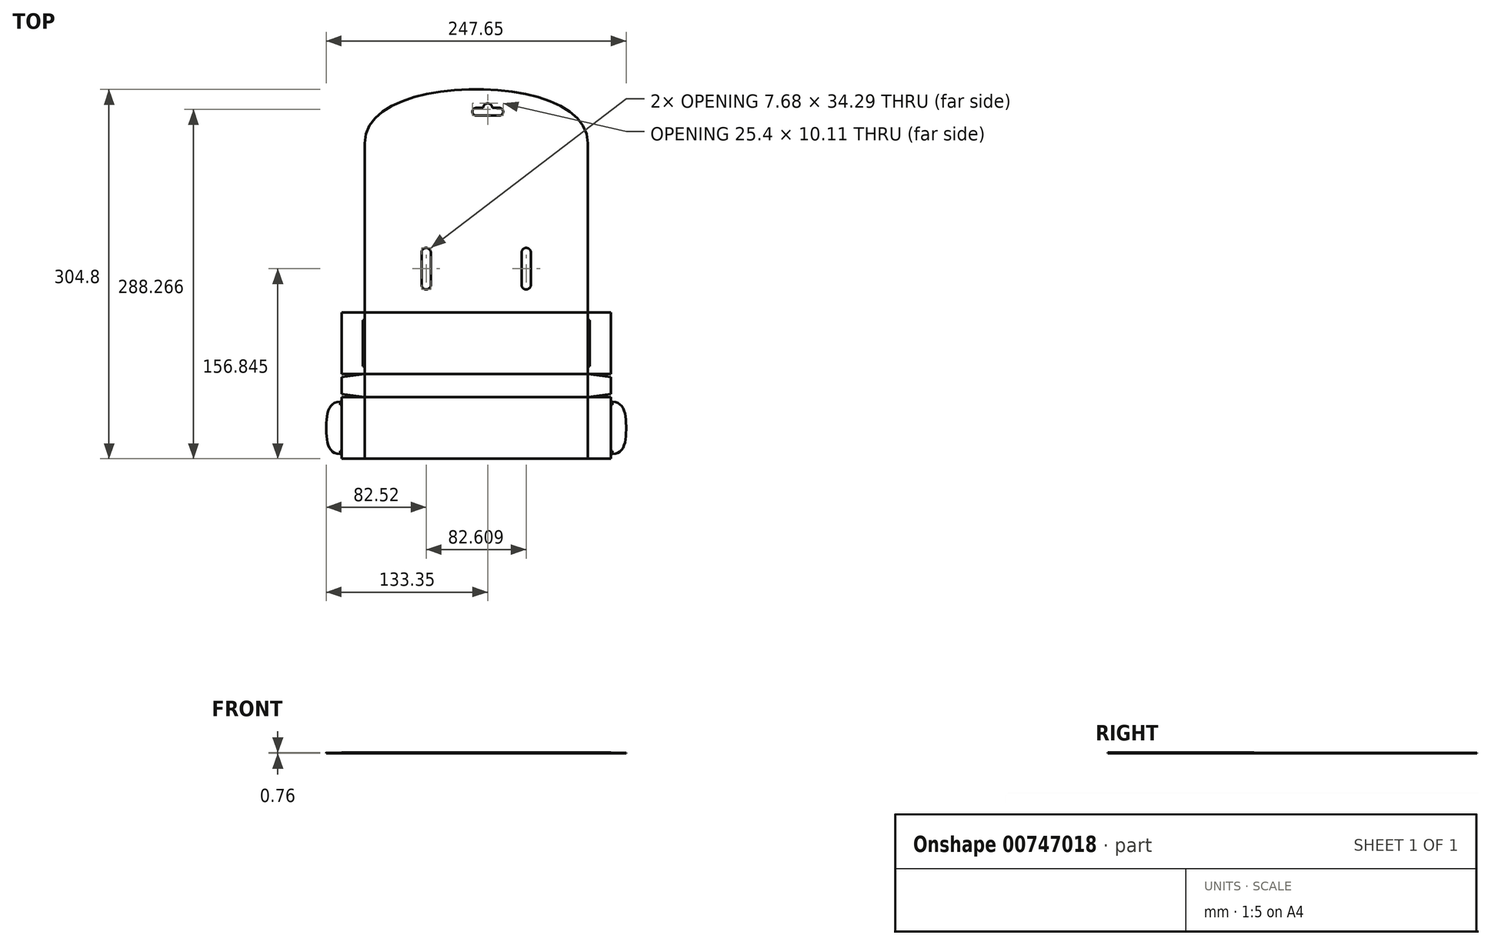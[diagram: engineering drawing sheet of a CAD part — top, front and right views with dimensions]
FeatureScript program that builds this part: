
annotation { "Feature Type Name" : "Feature", "Feature Type Description" : "" }
export const myFeature = defineFeature(function(context is Context, id is Id, definition is map)
    precondition{}
    {
        {
            var Q0;
            Q0=qCreatedBy(makeId("Top.planeOp"),FACE);
            var sketch = newSketch(context, id + "F0", { "sketchPlane" : qUnion([Q0])});
            skLineSegment(sketch, "E0", {"start": v(0, 0) * mm, "end": v(184.15, 0) * mm});
            skLineSegment(sketch, "E1", {"start": v(184.15, 0) * mm, "end": v(184.15, 50.8) * mm});
            skLineSegment(sketch, "E2", {"start": v(184.15, 50.8) * mm, "end": v(203.2, 50.8) * mm});
            skLineSegment(sketch, "E3", {"start": v(203.2, 50.8) * mm, "end": v(203.2, 0) * mm});
            skLineSegment(sketch, "E4", {"start": v(203.2, 0) * mm, "end": v(184.15, 0) * mm});
            skLineSegment(sketch, "E5", {"start": v(184.15, 50.8) * mm, "end": v(0, 50.8) * mm});
            skLineSegment(sketch, "E6", {"start": v(0, 50.8) * mm, "end": v(0, 0) * mm});
            skLineSegment(sketch, "E7", {"start": v(0, 50.8) * mm, "end": v(-19.05, 50.8) * mm});
            skLineSegment(sketch, "E8", {"start": v(-19.05, 50.8) * mm, "end": v(-19.05, 0) * mm});
            skLineSegment(sketch, "E9", {"start": v(-19.05, 0) * mm, "end": v(0, 0) * mm});
            skLineSegment(sketch, "E10", {"start": v(0, 50.8) * mm, "end": v(0, 69.85) * mm});
            skLineSegment(sketch, "E11", {"start": v(0, 69.85) * mm, "end": v(184.15, 69.85) * mm});
            skLineSegment(sketch, "E12", {"start": v(184.15, 69.85) * mm, "end": v(184.15, 50.8) * mm});
            skLineSegment(sketch, "E13", {"start": v(-19.05, 67.3) * mm, "end": v(-19.05, 53.34) * mm});
            skLineSegment(sketch, "E14", {"start": v(-19.05, 67.3) * mm, "end": v(0, 69.85) * mm});
            skLineSegment(sketch, "E15", {"start": v(-19.05, 53.34) * mm, "end": v(0, 50.8) * mm});
            skLineSegment(sketch, "E16", {"start": v(0, 69.85) * mm, "end": v(0, 260.35) * mm});
            skLineSegment(sketch, "E17", {"start": v(0, 260.35) * mm, "end": v(184.15, 260.35) * mm, "construction": true});
            skLineSegment(sketch, "E18", {"start": v(184.15, 260.35) * mm, "end": v(184.15, 69.85) * mm});
            skLineSegment(sketch, "E19.0", {"start": v(0, 120.65) * mm, "end": v(203.2, 120.65) * mm});
            skLineSegment(sketch, "E20", {"start": v(0, 120.65) * mm, "end": v(-19.05, 120.65) * mm});
            skLineSegment(sketch, "E21", {"start": v(-19.05, 120.65) * mm, "end": v(-19.05, 69.85) * mm});
            skLineSegment(sketch, "E22", {"start": v(-19.05, 69.85) * mm, "end": v(0, 69.85) * mm});
            skLineSegment(sketch, "E23", {"start": v(92.08, 0) * mm, "end": v(92.08, 260.35) * mm, "construction": true});
            skLineSegment(sketch, "E24.MirrorCS", {"start": v(203.2, 67.3) * mm, "end": v(203.2, 53.34) * mm});
            skLineSegment(sketch, "E25.MirrorCS", {"start": v(203.2, 67.3) * mm, "end": v(184.15, 69.85) * mm});
            skLineSegment(sketch, "E26.MirrorCS", {"start": v(203.2, 53.34) * mm, "end": v(184.15, 50.8) * mm});
            skLineSegment(sketch, "E27.MirrorCS", {"start": v(203.2, 69.85) * mm, "end": v(184.15, 69.85) * mm});
            skLineSegment(sketch, "E28.MirrorCS", {"start": v(203.2, 120.65) * mm, "end": v(203.2, 69.85) * mm});
            skLineSegment(sketch, "E29.MirrorCS", {"start": v(184.15, 120.65) * mm, "end": v(203.2, 120.65) * mm});
            skFitSpline(sketch, "E30", {"points": [v(0, 260.35) * mm, v(92.08, 304.8) * mm, v(184.15, 260.35) * mm], "startDerivative": vector(0, 185.57) * mm, "endDerivative": vector(0, -185.57) * mm});
            skLineSegment(sketch, "E31", {"start": v(133.4, 224.8) * mm, "end": v(133.4, 174) * mm});
            skLineSegment(sketch, "E32", {"start": v(127.06, 231.14) * mm, "end": v(57.2, 231.14) * mm});
            skLineSegment(sketch, "E33", {"start": v(50.86, 224.8) * mm, "end": v(50.86, 174) * mm});
            skLineSegment(sketch, "E34.0", {"start": v(129.54, 170.18) * mm, "end": v(129.54, 143.51) * mm});
            skLineSegment(sketch, "E35.0", {"start": v(137.22, 170.17) * mm, "end": v(137.16, 143.5) * mm});
            skLineSegment(sketch, "E36", {"start": v(133.35, 139.7) * mm, "end": v(133.35, 139.7) * mm});
            skLineSegment(sketch, "E37", {"start": v(133.35, 173.99) * mm, "end": v(133.4, 174) * mm});
            skLineSegment(sketch, "E38.MirrorCS", {"start": v(54.6, 170.18) * mm, "end": v(54.61, 143.51) * mm});
            skLineSegment(sketch, "E39.MirrorCS", {"start": v(46.93, 170.17) * mm, "end": v(47, 143.5) * mm});
            skLineSegment(sketch, "E40.MirrorCS", {"start": v(50.8, 139.7) * mm, "end": v(50.8, 139.7) * mm});
            skLineSegment(sketch, "E41.MirrorCS", {"start": v(50.8, 173.99) * mm, "end": v(50.74, 174) * mm});
            skPoint(sketch, "E42.visualSharp", {"position": v(129.54, 173.99) * mm});
            skArc(sketch, "E42.filletArc", {"start": v(133.35, 173.99) * mm, "mid": v(130.66, 172.87) * mm, "end": v(129.54, 170.18) * mm});
            skPoint(sketch, "E43.visualSharp", {"position": v(137.23, 174) * mm});
            skArc(sketch, "E43.filletArc", {"start": v(137.22, 170.17) * mm, "mid": v(136.1, 172.87) * mm, "end": v(133.4, 174) * mm});
            skPoint(sketch, "E44.visualSharp", {"position": v(129.54, 139.7) * mm});
            skArc(sketch, "E44.filletArc", {"start": v(129.54, 143.51) * mm, "mid": v(130.66, 140.82) * mm, "end": v(133.35, 139.7) * mm});
            skPoint(sketch, "E45.visualSharp", {"position": v(137.15, 139.7) * mm});
            skArc(sketch, "E45.filletArc", {"start": v(133.35, 139.7) * mm, "mid": v(136.04, 140.81) * mm, "end": v(137.16, 143.5) * mm});
            skPoint(sketch, "E46.visualSharp", {"position": v(54.6, 173.99) * mm});
            skArc(sketch, "E46.filletArc", {"start": v(54.6, 170.18) * mm, "mid": v(53.5, 172.87) * mm, "end": v(50.8, 173.99) * mm});
            skPoint(sketch, "E47.visualSharp", {"position": v(46.92, 174) * mm});
            skArc(sketch, "E47.filletArc", {"start": v(50.74, 174) * mm, "mid": v(48.04, 172.87) * mm, "end": v(46.93, 170.17) * mm});
            skPoint(sketch, "E48.visualSharp", {"position": v(47, 139.7) * mm});
            skArc(sketch, "E48.filletArc", {"start": v(47, 143.5) * mm, "mid": v(48.1, 140.81) * mm, "end": v(50.8, 139.7) * mm});
            skPoint(sketch, "E49.visualSharp", {"position": v(54.61, 139.7) * mm});
            skArc(sketch, "E49.filletArc", {"start": v(50.8, 139.7) * mm, "mid": v(53.5, 140.82) * mm, "end": v(54.61, 143.51) * mm});
            skPoint(sketch, "E50.visualSharp", {"position": v(50.86, 231.14) * mm});
            skArc(sketch, "E50.filletArc", {"start": v(57.2, 231.14) * mm, "mid": v(52.72, 229.28) * mm, "end": v(50.86, 224.8) * mm});
            skPoint(sketch, "E51.visualSharp", {"position": v(133.4, 231.14) * mm});
            skArc(sketch, "E51.filletArc", {"start": v(133.4, 224.8) * mm, "mid": v(131.55, 229.28) * mm, "end": v(127.06, 231.14) * mm});
            skLineSegment(sketch, "E52", {"start": v(184.15, 114.3) * mm, "end": v(185.74, 114.3) * mm});
            skLineSegment(sketch, "E53", {"start": v(185.74, 114.3) * mm, "end": v(185.74, 76.2) * mm});
            skLineSegment(sketch, "E54", {"start": v(185.74, 76.2) * mm, "end": v(184.15, 76.2) * mm});
            skLineSegment(sketch, "E55.MirrorCS", {"start": v(-1.59, 114.3) * mm, "end": v(-1.59, 76.2) * mm});
            skLineSegment(sketch, "E56.MirrorCS", {"start": v(0, 114.3) * mm, "end": v(-1.59, 114.3) * mm});
            skLineSegment(sketch, "E57.MirrorCS", {"start": v(-1.59, 76.2) * mm, "end": v(0, 76.2) * mm});
            skLineSegment(sketch, "E58", {"start": v(-19.05, 3.81) * mm, "end": v(-19.05, 0) * mm});
            skFitSpline(sketch, "E59", {"points": [v(-20.32, 46.99) * mm, v(-31.75, 25.4) * mm, v(-20.32, 3.8) * mm], "startDerivative": vector(-60.96, -1.37) * mm, "endDerivative": vector(60.96, -0.05) * mm});
            skLineSegment(sketch, "E60.0", {"start": v(-20.32, 44.45) * mm, "end": v(-19.05, 44.45) * mm});
            skLineSegment(sketch, "E61.0", {"start": v(-20.32, 6.35) * mm, "end": v(-19.05, 6.35) * mm});
            skLineSegment(sketch, "E62", {"start": v(-20.32, 46.99) * mm, "end": v(-20.32, 44.45) * mm});
            skLineSegment(sketch, "E63", {"start": v(-20.32, 3.8) * mm, "end": v(-20.32, 6.35) * mm});
            skFitSpline(sketch, "E64.MirrorCS", {"points": [v(204.47, 46.99) * mm, v(215.9, 25.4) * mm, v(204.47, 3.8) * mm], "startDerivative": vector(60.96, -1.37) * mm, "endDerivative": vector(-60.96, -0.05) * mm});
            skLineSegment(sketch, "E65.MirrorCS", {"start": v(204.47, 46.99) * mm, "end": v(204.47, 44.45) * mm});
            skLineSegment(sketch, "E66.MirrorCS", {"start": v(204.47, 44.45) * mm, "end": v(203.2, 44.45) * mm});
            skLineSegment(sketch, "E67.MirrorCS", {"start": v(204.47, 3.8) * mm, "end": v(204.47, 6.35) * mm});
            skLineSegment(sketch, "E68.MirrorCS", {"start": v(204.47, 6.35) * mm, "end": v(203.2, 6.35) * mm});
            skLineSegment(sketch, "E69", {"start": v(88.9, 286.39) * mm, "end": v(88.9, 286.39) * mm});
            skLineSegment(sketch, "E70", {"start": v(92.08, 283.21) * mm, "end": v(111.13, 283.21) * mm});
            skLineSegment(sketch, "E71", {"start": v(114.3, 286.39) * mm, "end": v(114.3, 286.39) * mm});
            skLineSegment(sketch, "E72", {"start": v(111.13, 289.56) * mm, "end": v(105.4, 289.56) * mm});
            skLineSegment(sketch, "E73", {"start": v(92.08, 289.56) * mm, "end": v(97.8, 289.56) * mm});
            skArc(sketch, "E74", {"start": v(105.4, 289.56) * mm, "mid": v(101.6, 293.32) * mm, "end": v(97.8, 289.56) * mm});
            skPoint(sketch, "E75.visualSharp", {"position": v(88.9, 289.56) * mm});
            skArc(sketch, "E75.filletArc", {"start": v(92.08, 289.56) * mm, "mid": v(89.83, 288.63) * mm, "end": v(88.9, 286.39) * mm});
            skPoint(sketch, "E76.visualSharp", {"position": v(88.9, 283.21) * mm});
            skArc(sketch, "E76.filletArc", {"start": v(88.9, 286.39) * mm, "mid": v(89.83, 284.14) * mm, "end": v(92.08, 283.21) * mm});
            skPoint(sketch, "E77.visualSharp", {"position": v(114.3, 289.56) * mm});
            skArc(sketch, "E77.filletArc", {"start": v(114.3, 286.39) * mm, "mid": v(113.37, 288.63) * mm, "end": v(111.13, 289.56) * mm});
            skPoint(sketch, "E78.visualSharp", {"position": v(114.3, 283.21) * mm});
            skArc(sketch, "E78.filletArc", {"start": v(111.13, 283.21) * mm, "mid": v(113.37, 284.14) * mm, "end": v(114.3, 286.39) * mm});
            skLineSegment(sketch, "E79", {"start": v(92.08, 304.8) * mm, "end": v(92.08, 260.35) * mm, "construction": true});
            skArc(sketch, "E80", {"start": v(50.8, 139.7) * mm, "mid": v(92.07, 126.94) * mm, "end": v(133.35, 139.7) * mm});
            skSolve(sketch);
        }
        {
            var Q0;
            {var subQ4=sQuery(id+"F0.wireOp",EDGE,"E11");Q0=makeQuery(id+"F0.imprint","IMPRINT",FACE,{"disambiguationData":[TD([[makeQuery(id+"F0.imprint","IMPRINT",EDGE,{"derivedFrom":subQ4}),1.0]])]});}
            var Q1;
            Q1=makeQuery(id+"F0.imprint","IMPRINT",FACE,{"disambiguationData":[TD([[makeQuery(id+"F0.imprint","IMPRINT",EDGE,{"derivedFrom":sQuery(id+"F0.wireOp",EDGE,"E10")}),1.0]])]});
            var Q2;
            Q2=makeQuery(id+"F0.imprint","IMPRINT",FACE,{"disambiguationData":[TD([[makeQuery(id+"F0.imprint","IMPRINT",EDGE,{"derivedFrom":sQuery(id+"F0.wireOp",EDGE,"E0")}),1.0]])]});
            var Q3;
            Q3=makeQuery(id+"F0.imprint","IMPRINT",FACE,{"disambiguationData":[TD([[makeQuery(id+"F0.imprint","IMPRINT",EDGE,{"derivedFrom":sQuery(id+"F0.wireOp",EDGE,"E12")}),1.0]])]});
            var Q4;
            Q4=makeQuery(id+"F0.imprint","IMPRINT",FACE,{"disambiguationData":[TD([[makeQuery(id+"F0.imprint","IMPRINT",EDGE,{"derivedFrom":sQuery(id+"F0.wireOp",EDGE,"E64.MirrorCS")}),-1.0]])]});
            var Q5;
            Q5=makeQuery(id+"F0.imprint","IMPRINT",FACE,{"disambiguationData":[TD([[makeQuery(id+"F0.imprint","IMPRINT",EDGE,{"derivedFrom":sQuery(id+"F0.wireOp",EDGE,"E59")}),1.0]])]});
            var Q6;
            Q6=makeQuery(id+"F0.imprint","IMPRINT",FACE,{"disambiguationData":[TD([[makeQuery(id+"F0.imprint","IMPRINT",EDGE,{"derivedFrom":sQuery(id+"F0.wireOp",EDGE,"E31")}),-1.0]])]});
            extrude(context, id + "F1", {"entities" : qUnion([Q0, Q1, Q2, Q3, Q4, Q5, Q6]), "depth" : 0.5 * mm, "offsetDistance" : 25.4 * mm});
        }
        {
            var Q0;
            Q0=makeQuery(id+"F0.imprint","IMPRINT",FACE,{"disambiguationData":[TD([[makeQuery(id+"F0.imprint","IMPRINT",EDGE,{"derivedFrom":sQuery(id+"F0.wireOp",EDGE,"E5")}),-1.0]])]});
            var Q1;
            {var subQ4=sQuery(id+"F0.wireOp",EDGE,"E27.MirrorCS");Q1=makeQuery(id+"F0.imprint","IMPRINT",FACE,{"disambiguationData":[TD([[makeQuery(id+"F0.imprint","IMPRINT",EDGE,{"derivedFrom":subQ4}),-1.0]])]});}
            var Q2;
            Q2=makeQuery(id+"F0.imprint","IMPRINT",FACE,{"disambiguationData":[TD([[makeQuery(id+"F0.imprint","IMPRINT",EDGE,{"derivedFrom":sQuery(id+"F0.wireOp",EDGE,"E1")}),-1.0]])]});
            var Q3;
            Q3=makeQuery(id+"F0.imprint","IMPRINT",FACE,{"disambiguationData":[TD([[makeQuery(id+"F0.imprint","IMPRINT",EDGE,{"derivedFrom":sQuery(id+"F0.wireOp",EDGE,"E6")}),-1.0]])]});
            var Q4;
            {var subQ0=sQuery(id+"F0.wireOp",EDGE,"E20");Q4=makeQuery(id+"F0.imprint","IMPRINT",FACE,{"disambiguationData":[TD([[makeQuery(id+"F0.imprint","IMPRINT",EDGE,{"derivedFrom":subQ0}),1.0]])]});}
            extrude(context, id + "F2", {"entities" : qUnion([Q0, Q1, Q2, Q3, Q4]), "depth" : 0.76 * mm, "offsetDistance" : 25.4 * mm});
        }
        {
            var Q0;
            {var subQ0=sQuery(id+"F0.wireOp",EDGE,"E19.0");Q0=makeQuery(id+"F0.imprint","IMPRINT",FACE,{"disambiguationData":[TD([[makeQuery(id+"F0.imprint","IMPRINT",EDGE,{"derivedFrom":subQ0}),1.0]])]});}
            extrude(context, id + "F3", {"entities" : qUnion([Q0]), "depth" : 0.38 * mm, "offsetDistance" : 25.4 * mm});
        }
    });
